# Revit family: Shower-Valve-KOHLER-NATEO-K-880A
name_source: partatom
category: Plumbing Fixtures
revit_build: Autodesk Revit 2017 (Build: 20160225_1515(x64)
units: mm (PartAtom-declared; Revit-internal decimal feet)

## family parameters
Cut with Voids When Loaded = No
Host = Face
OmniClass Number = 23.31.17.00
OmniClass Title = Showers
Part Type = Normal
Room Calculation Point = No
Round Connector Dimension = Use Diameter
Shared = No

## types (6) — shared parameters
ADA Compliant = No
Assembly Code = D2010700
CW Connection = Yes
Cold Water Inlet = Cold Water Inlet
Date Modified = 08/06/2020
Default Elevation = 48 1/16"
Description = Recessed Shower Valve
Drain Included = No
Flow Rate = 0 GPM
HW Connection = Yes
Height = 6 1/2"
Hot Water Inlet = Hot Water Inlet
Length = 5 3/8"
Manufacturer = KOHLER Co.
Master Format 2014 = 22 42 23
Master Format 2014 Name = Residential Showers
Material = Metal construction
Pressure = 0.00 psi
Product Name = NATEO
Tempered water outlet 2 = Tempered water outlet 2
Tempered watet outlet 1 = Tempered watet outlet 1
URL = https://www.kohlerasiapacific.com
Vent Connection = No
Waste Connection = No
Waste Water Outlet = Waste Water Outlet
WaterSense Certified = No
Width = 3 7/16"

## per-type parameters (varying)
| type | Finish | Model | Type |
| CP- Polished Chrome | Kohler-Metal-CP-Polished_Chrome | K-880A-CP | 1 |
| 2BZ- Oil-Rubbed Bronze | Kohler-Metal-2BZ-Oil_Rubbed_Bronze | K-880A-2BZ | 2 |
| BL- Matte Black | Kohler-Metal-BL-Matte_Black | K-880A-BL | 3 |
| BV-Brushed Bronze | Kohler-Metal-BV-Brushed_Bronze | K-880A-BV | 4 |
| RGD- Polished Rose Gold | Kohler-Metal-RGD-Polished_Rose_Gold | K-880A-RGD | 5 |
| TT- Vibrant Titanium | Kohler-Metal-TT-Vibrant_Titanium | K-880A-TT | 6 |

## geometry (parser evidence)
native form markers: Sweep x4
no freeform markers — native parametric forms only
